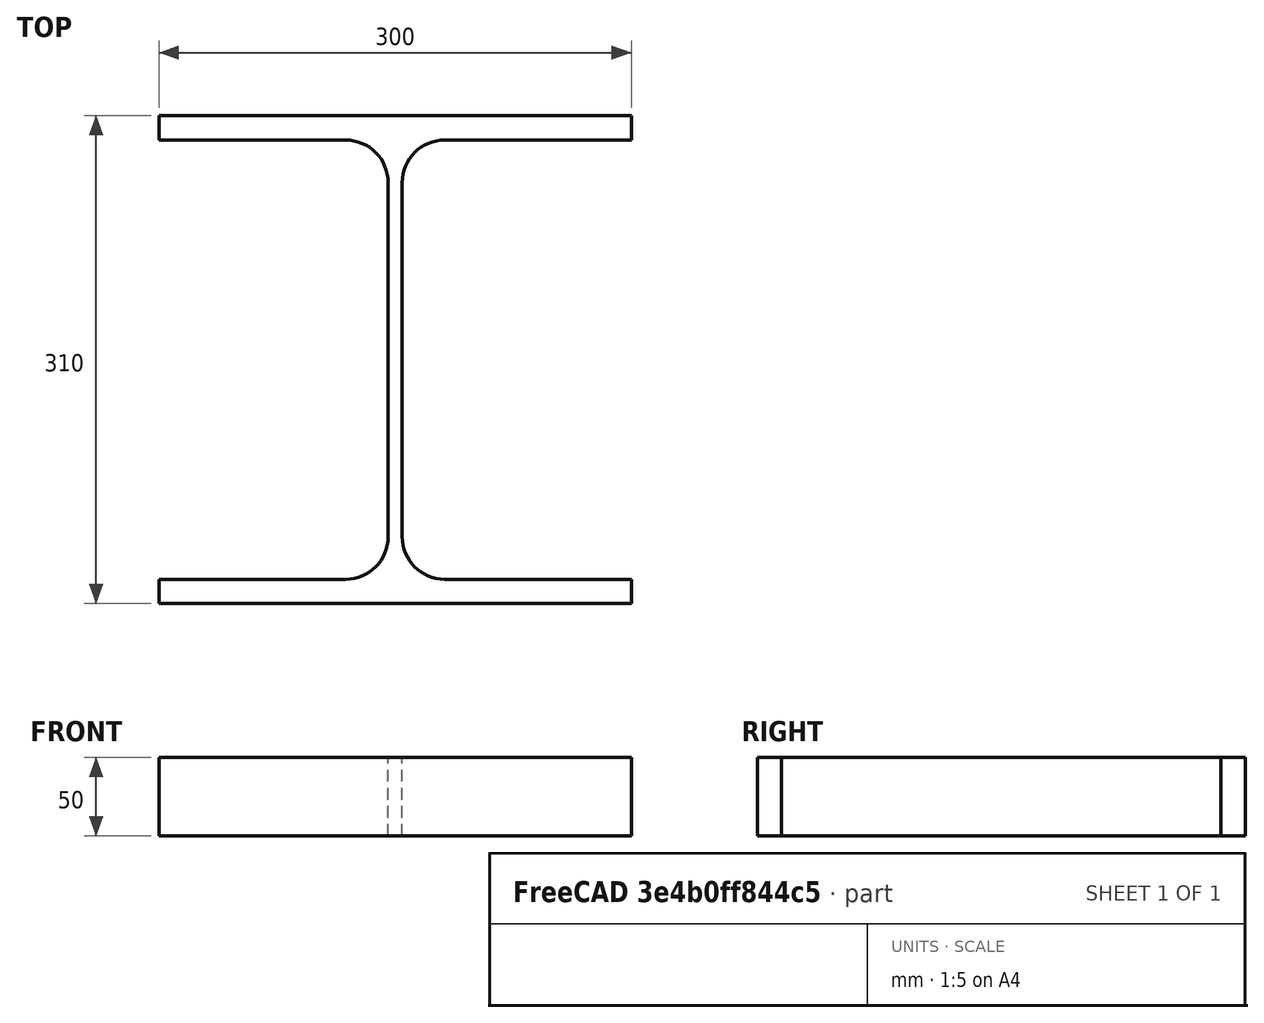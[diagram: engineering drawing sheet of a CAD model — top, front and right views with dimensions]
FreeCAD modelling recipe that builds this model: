
FCSTD DOCUMENT  (FreeCAD 0.15R4671 (Git))
Label: HE-A-Profile 320 DIN1025-3 S235JR
License: All rights reserved
LicenseURL: http://en.wikipedia.org/wiki/All_rights_reserved
objects: Sketcher::SketchObject×1, Part::Extrusion×1
note: 2 computed .brp shape members not serialized (recipe doc carries the construction recipe); baked Part::Feature solids carry a one-line shape summary decoded from their .brp

FEATURE [Sketcher::SketchObject] Sketch
  sketch-geometry (16):
    g0: LineSegment StartX=4.5 StartY=-112.5 StartZ=0 EndX=4.5 EndY=112.5 EndZ=0
    g1: LineSegment StartX=31.5 StartY=139.5 StartZ=0 EndX=150 EndY=139.5 EndZ=0
    g2: LineSegment StartX=150 StartY=139.5 StartZ=0 EndX=150 EndY=155 EndZ=0
    g3: LineSegment StartX=150 StartY=155 StartZ=0 EndX=-150 EndY=155 EndZ=0
    g4: LineSegment StartX=-150 StartY=155 StartZ=0 EndX=-150 EndY=139.5 EndZ=0
    g5: LineSegment StartX=-150 StartY=139.5 StartZ=0 EndX=-31.5 EndY=139.5 EndZ=0
    g6: LineSegment StartX=-4.5 StartY=112.5 StartZ=0 EndX=-4.5 EndY=-112.5 EndZ=0
    g7: LineSegment StartX=-31.5 StartY=-139.5 StartZ=0 EndX=-150 EndY=-139.5 EndZ=0
    g8: LineSegment StartX=-150 StartY=-139.5 StartZ=0 EndX=-150 EndY=-155 EndZ=0
    g9: LineSegment StartX=-150 StartY=-155 StartZ=0 EndX=150 EndY=-155 EndZ=0
    g10: LineSegment StartX=150 StartY=-155 StartZ=0 EndX=150 EndY=-139.5 EndZ=0
    g11: LineSegment StartX=150 StartY=-139.5 StartZ=0 EndX=31.5 EndY=-139.5 EndZ=0
    g12: ArcOfCircle CenterX=31.5 CenterY=112.5 CenterZ=0 NormalX=0 NormalY=0 NormalZ=1 Radius=27 StartAngle=1.5708 EndAngle=3.14159
    g13: ArcOfCircle CenterX=31.5 CenterY=-112.5 CenterZ=0 NormalX=0 NormalY=0 NormalZ=1 Radius=27 StartAngle=3.14159 EndAngle=4.71239
    g14: ArcOfCircle CenterX=-31.5 CenterY=112.5 CenterZ=0 NormalX=0 NormalY=0 NormalZ=1 Radius=27 StartAngle=0 EndAngle=1.5708
    g15: ArcOfCircle CenterX=-31.5 CenterY=-112.5 CenterZ=0 NormalX=0 NormalY=0 NormalZ=1 Radius=27 StartAngle=4.71239 EndAngle=6.28319
  constraints (42):
    c: Vertical(g0)
    c: Coincident(g2,g1)
    c: Vertical(g2)
    c: Coincident(g3,g2)
    c: Coincident(g4,g3)
    c: Vertical(g4)
    c: Coincident(g5,g4)
    c: Horizontal(g5)
    c: Vertical(g6)
    c: Horizontal(g7)
    c: Coincident(g8,g7)
    c: Vertical(g8)
    c: Coincident(g9,g8)
    c: Horizontal(g9)
    c: Coincident(g10,g9)
    c: Vertical(g10)
    c: Coincident(g11,g10)
    c: Horizontal(g11)
    c: Tangent(g1,g12) = 1.5708
    c: Tangent(g0,g12) = 1.5708
    c: Tangent(g0,g13) = 1.5708
    c: Tangent(g11,g13) = 1.5708
    c: Tangent(g5,g14) = 1.5708
    c: Tangent(g6,g14) = 1.5708
    c: Tangent(g6,g15) = 1.5708
    c: Tangent(g7,g15) = 1.5708
    c: Equal(g3,g9)
    c: Equal(g2,g4)
    c: Equal(g4,g8)
    c: Equal(g8,g10)
    c: Equal(g12,g14)
    c: Equal(g14,g15)
    c: Equal(g15,g13)
    c: Symmetric(g2,g3,g-2)
    c: Symmetric(g9,g8,g-2)
    c: Symmetric(g0,g6,g-2)
    c: Symmetric(g2,g9,g-1)
    c: DistanceY(g2,g9) = -310
    c: DistanceX(g3) = -300
    c: DistanceX(g0,g6) = -9
    c: DistanceY(g2) = 15.5
    c: Radius(g12) = 27
FEATURE [Part::Extrusion] Extrude  label="HE-A-Profile 320 DIN1025-3 S235JR"
  Base = -> Sketch
  Dir = (0,0,50)
  Solid = true
